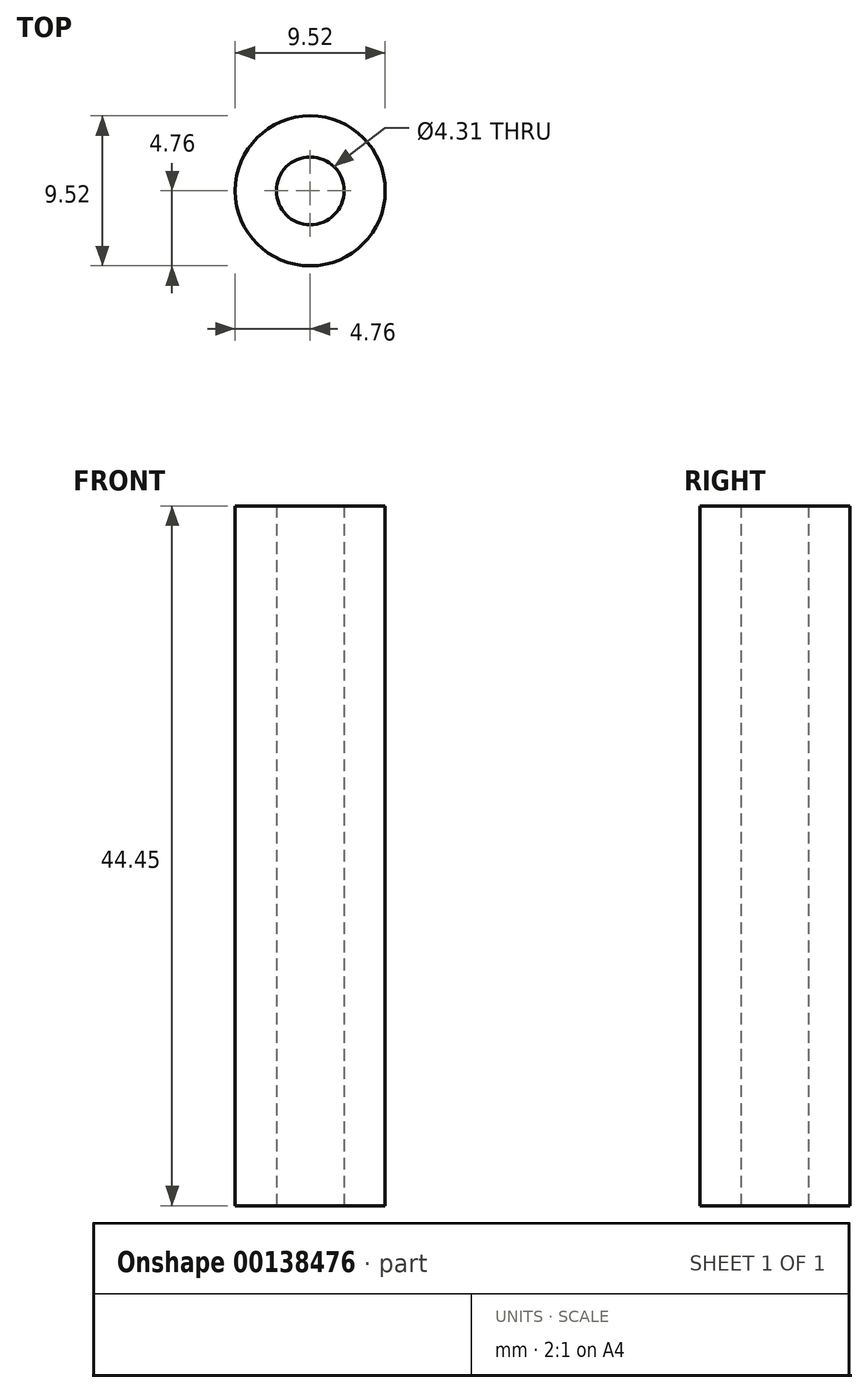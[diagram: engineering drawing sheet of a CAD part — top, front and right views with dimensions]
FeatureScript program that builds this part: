
annotation { "Feature Type Name" : "Feature", "Feature Type Description" : "" }
export const myFeature = defineFeature(function(context is Context, id is Id, definition is map)
    precondition{}
    {
        {
            var Q0;
            Q0=qCreatedBy(makeId("Top.planeOp"),FACE);
            var sketch = newSketch(context, id + "F0", { "sketchPlane" : qUnion([Q0])});
            skCircle(sketch, "E0", {"center": v(0, 0) * mm, "radius": 2.15 * mm});
            skCircle(sketch, "E1", {"center": v(0, 0) * mm, "radius": 4.76 * mm});
            skSolve(sketch);
        }
        {
            var Q0;
            Q0 = qSketchRegion(id + "F0", true);
            extrude(context, id + "F1", {"entities" : qUnion([Q0]), "depth" : 44.45 * mm});
        }
    });
